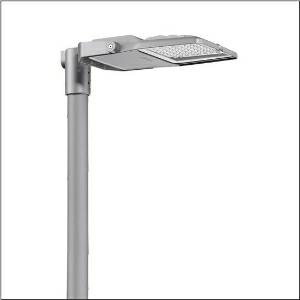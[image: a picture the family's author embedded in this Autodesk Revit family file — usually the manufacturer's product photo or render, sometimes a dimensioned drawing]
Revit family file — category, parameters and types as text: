
# Revit family: floodlight_fl_21_mini___pl61_5xa7776d4c3a_5b5f
name_source: partatom
category: Lighting Fixtures
units: mm (PartAtom-declared; Revit-internal decimal feet)

## family parameters
Cut with Voids When Loaded = No
Host = Face
Light Source = No
Part Type = Normal
Room Calculation Point = No
Round Connector Dimension = Use Diameter
Shared = No

## types (1)
- --- (1 x LED, 18260 lm, 142.9 W, 4000K)
    Apparent Load = 143 VA
    CIE Flux Codes = 33 65 98 100 100
    Color Rendering = 70
    Color Temperature = 4000K
    Default Elevation = 1800 mm
    Description = Floodlight FL 21 mini, floodlight, primary light control with lens, of PMMA, primary optical cover: protective disc, of toughened safety glass, transparent, light distribution: PL61, light emission: direct distribution, installation type: surface-mounted, LED, High Power LED, rated luminous flux: 18.260lm, luminous efficacy: 128lm/W, light colour: 740, colour temperature: 4000K, control gear: D4iSmart Interface (Zhaga), control: overheat protection, constant luminous flux control, time-dependent luminous flux control, flexible luminous flux parameterisation, pre-setting: logarithmic dimming characteristic, with terminal, 6-pole, mains connection: 220..240V, AC, 50/60Hz, start of lifetime: 143W, end of service life: 151W, reduction: 63W, mast bracket, of diecast aluminium, powder-coated, Siteco® metallic grey (DB 702S), corrosivity category C5 mid according to DIN EN ISO 12944, suitable for swimming pools, chlorine-resistant, sealing non-destructively replaceable, mast bracket, of steel, galvanised, powder-coated, Siteco® metallic grey (DB 702S), Smart Interface below and above, protection rating (complete): IP66, insulation class (complete): insulation class II (safety insulation), certification: CE, ENEC, VDE, protection symbol: D, impact resistance: IK08, permissible operating ambient temperature: -40..+40°C, permissible operating ambient temperature for outdoor applications: -40..+50°C, standard: DIN EN 12944, LABS conformity tested according to VDMA 24364:2018-05, packaging unit: 1 piece

Light Distribution: PL61
    Height = 70 mm
    Lamp = 1 x LED
    Lamp Light Flux = 18260 lm
    Lamp Power = 142.9 W
    Lamp count = 1
    Length = 485 mm
    Luminous efficacy = 128 lm/W
    Manufacturer = Siteco
    ModVariant = No
    Model = 5XA7776D4C3A
    Number of Poles = 1
    OnlyDefault = Yes
    Power Factor = 1
    Product Name = Floodlight FL 21 mini | PL61
    Product group = floodlight | pylon annexe
    ProductGroupID = 6201
    Protection Class = Protection class II
    Protection Degree = IP 66
    RLX_Detail_Level = 1
    RLX_Emergency_Light_Flux = 0 lm
    RLX_Emergency_Type = 0
    RLX_Emergency_Type_DB = No
    RlxData = <blob elided: 101397 chars, md5=208a051a>
    Socket = socket
    Standby Power = 0 W
    System Light Flux = 18260 lm
    System Power = 143 W
    Type Comments = factory setting: luminous flux: 100 % | dim-lin: 254 | 730 mA
    Type Image = l_1007125.jpg
    URL = http://relux.com
    VarID = @adj_121865
    Voltage = 0 V
    Weight = 0.00 kg
    Width = 337 mm

## geometry (parser evidence)
native form markers: Blend x4, Sweep x12
no freeform markers — native parametric forms only
